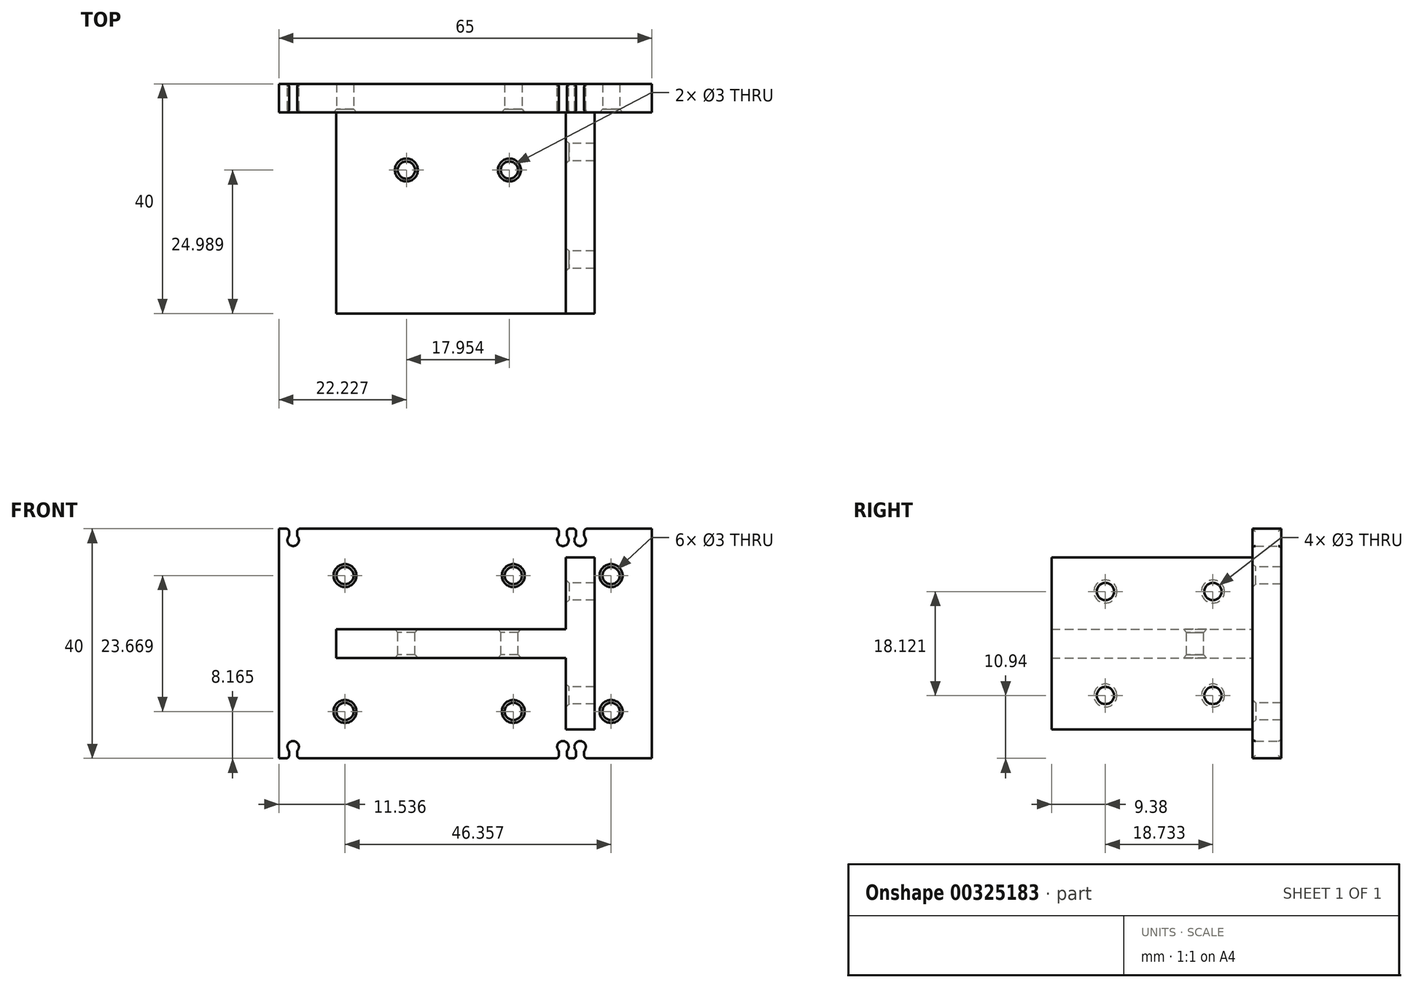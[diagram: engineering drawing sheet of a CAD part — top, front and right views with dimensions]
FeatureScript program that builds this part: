
annotation { "Feature Type Name" : "Feature", "Feature Type Description" : "" }
export const myFeature = defineFeature(function(context is Context, id is Id, definition is map)
    precondition{}
    {
        {
            var Q0;
            Q0=qCreatedBy(makeId("Front.planeOp"),FACE);
            var sketch = newSketch(context, id + "F0", { "sketchPlane" : qUnion([Q0])});
            skLineSegment(sketch, "E0.bottom", {"start": v(0, 0) * mm, "end": v(-55, 0) * mm});
            skLineSegment(sketch, "E0.top", {"start": v(0, 20) * mm, "end": v(-55, 20) * mm});
            skLineSegment(sketch, "E0.left", {"start": v(0, 0) * mm, "end": v(0, 20) * mm});
            skLineSegment(sketch, "E0.right", {"start": v(-55, 0) * mm, "end": v(-55, 20) * mm});
            skCircle(sketch, "E1", {"center": v(-52.5, 17.98) * mm, "radius": 1 * mm});
            skLineSegment(sketch, "E2", {"start": v(-52.5, 17.98) * mm, "end": v(-51.5, 17.98) * mm, "construction": true});
            skLineSegment(sketch, "E3", {"start": v(-52.5, 17.98) * mm, "end": v(-51.8, 18.69) * mm, "construction": true});
            skLineSegment(sketch, "E4", {"start": v(-51.8, 18.69) * mm, "end": v(-51.8, 20) * mm});
            skLineSegment(sketch, "E5", {"start": v(-53.2, 20) * mm, "end": v(-53.2, 18.69) * mm});
            skCircle(sketch, "E6", {"center": v(-2.5, 17.98) * mm, "radius": 1 * mm});
            skLineSegment(sketch, "E7", {"start": v(-2.5, 17.98) * mm, "end": v(-1.5, 17.98) * mm, "construction": true});
            skLineSegment(sketch, "E8", {"start": v(-2.5, 17.98) * mm, "end": v(-1.8, 18.69) * mm, "construction": true});
            skLineSegment(sketch, "E9", {"start": v(-1.8, 18.69) * mm, "end": v(-1.8, 20) * mm});
            skLineSegment(sketch, "E10", {"start": v(-3.2, 20) * mm, "end": v(-3.2, 18.69) * mm});
            skLineSegment(sketch, "E11.bottom", {"start": v(0, 0) * mm, "end": v(10, 0) * mm});
            skLineSegment(sketch, "E11.top", {"start": v(0, 20) * mm, "end": v(10, 20) * mm});
            skLineSegment(sketch, "E11.right", {"start": v(10, 0) * mm, "end": v(10, 20) * mm});
            skCircle(sketch, "E12", {"center": v(-5.5, 17.98) * mm, "radius": 1 * mm});
            skLineSegment(sketch, "E13", {"start": v(-5.5, 17.98) * mm, "end": v(-4.5, 17.98) * mm, "construction": true});
            skLineSegment(sketch, "E14", {"start": v(-5.5, 17.98) * mm, "end": v(-4.8, 18.69) * mm, "construction": true});
            skLineSegment(sketch, "E15", {"start": v(-4.8, 18.69) * mm, "end": v(-4.8, 20) * mm});
            skLineSegment(sketch, "E16", {"start": v(-6.2, 20) * mm, "end": v(-6.2, 18.69) * mm});
            skSolve(sketch);
        }
        {
            var Q0;
            Q0=makeQuery(id+"F0.imprint","IMPRINT",FACE,{"disambiguationData":[TD([[makeQuery(id+"F0.imprint","IMPRINT",EDGE,{"derivedFrom":sQuery(id+"F0.wireOp",EDGE,"E0.bottom")}),-1.0]])]});
            var Q1;
            Q1=makeQuery(id+"F0.imprint","IMPRINT",FACE,{"disambiguationData":[TD([[makeQuery(id+"F0.imprint","IMPRINT",EDGE,{"derivedFrom":sQuery(id+"F0.wireOp",EDGE,"E11.bottom")}),1.0]])]});
            extrude(context, id + "F1", {"entities" : qUnion([Q0, Q1]), "depth" : 5 * mm});
        }
        {
            var Q0;
            Q0=makeQuery(id+"F1.opExtrude","SWEPT_FACE",FACE,{"disambiguationData":[OSD([sQuery(id+"F0.wireOp",EDGE,"E4")])]});
            var Q1;
            Q1=makeQuery(id+"F1.opExtrude","SWEPT_FACE",FACE,{"disambiguationData":[OSD([sQuery(id+"F0.wireOp",EDGE,"E1")])]});
            var Q2;
            Q2=makeQuery(id+"F1.opExtrude","SWEPT_FACE",FACE,{"disambiguationData":[OSD([sQuery(id+"F0.wireOp",EDGE,"E5")])]});
            var Q3;
            Q3=makeQuery(id+"F1.opExtrude","CAP_EDGE",EDGE,{"disambiguationData":[OSD([sQuery(id+"F0.wireOp",EDGE,"E1")])],"isStart":false});
            var Q4;
            Q4=makeQuery(id+"F1.opExtrude","SWEPT_EDGE",EDGE,{"disambiguationData":[OSD([sQuery(id+"F0.wireOp",EDGE,"E0.top"),sQuery(id+"F0.wireOp",EDGE,"E4")])]});
            var Q5;
            Q5=makeQuery(id+"F1.opExtrude","SWEPT_EDGE",EDGE,{"disambiguationData":[OSD([sQuery(id+"F0.wireOp",EDGE,"E0.top"),sQuery(id+"F0.wireOp",EDGE,"E5")])]});
            var Q6;
            Q6=makeQuery(id+"F1.opExtrude","SWEPT_EDGE",EDGE,{"disambiguationData":[OSD([sQuery(id+"F0.wireOp",EDGE,"E1"),sQuery(id+"F0.wireOp",EDGE,"E5")])]});
            var Q7;
            Q7=makeQuery(id+"F1.opExtrude","SWEPT_EDGE",EDGE,{"disambiguationData":[OSD([sQuery(id+"F0.wireOp",EDGE,"E1"),sQuery(id+"F0.wireOp",EDGE,"E4")])]});
            var Q8;
            Q8=makeQuery(id+"F1.opExtrude","CAP_EDGE",EDGE,{"disambiguationData":[OSD([sQuery(id+"F0.wireOp",EDGE,"E5")])],"isStart":false});
            var Q9;
            Q9=makeQuery(id+"F1.opExtrude","CAP_EDGE",EDGE,{"disambiguationData":[OSD([sQuery(id+"F0.wireOp",EDGE,"E1")])],"isStart":true});
            var Q10;
            Q10=makeQuery(id+"F1.opExtrude","CAP_EDGE",EDGE,{"disambiguationData":[OSD([sQuery(id+"F0.wireOp",EDGE,"E4")])],"isStart":false});
            var Q11;
            Q11=makeQuery(id+"F1.opExtrude","CAP_EDGE",EDGE,{"disambiguationData":[OSD([sQuery(id+"F0.wireOp",EDGE,"E4")])],"isStart":true});
            var Q12;
            Q12=makeQuery(id+"F1.opExtrude","CAP_EDGE",EDGE,{"disambiguationData":[OSD([sQuery(id+"F0.wireOp",EDGE,"E5")])],"isStart":true});
            var Q13;
            Q13=makeQuery(id+"F1.opExtrude","SWEPT_FACE",FACE,{"disambiguationData":[OSD([sQuery(id+"F0.wireOp",EDGE,"E9")])]});
            var Q14;
            Q14=makeQuery(id+"F1.opExtrude","SWEPT_FACE",FACE,{"disambiguationData":[OSD([sQuery(id+"F0.wireOp",EDGE,"E10")])]});
            var Q15;
            Q15=makeQuery(id+"F1.opExtrude","CAP_EDGE",EDGE,{"disambiguationData":[OSD([sQuery(id+"F0.wireOp",EDGE,"E6")])],"isStart":false});
            var Q16;
            Q16=makeQuery(id+"F1.opExtrude","SWEPT_FACE",FACE,{"disambiguationData":[OSD([sQuery(id+"F0.wireOp",EDGE,"E6")])]});
            var Q17;
            Q17=makeQuery(id+"F1.opExtrude","SWEPT_EDGE",EDGE,{"disambiguationData":[OSD([sQuery(id+"F0.wireOp",EDGE,"E6"),sQuery(id+"F0.wireOp",EDGE,"E9")])]});
            var Q18;
            Q18=makeQuery(id+"F1.opExtrude","SWEPT_EDGE",EDGE,{"disambiguationData":[OSD([sQuery(id+"F0.wireOp",EDGE,"E6"),sQuery(id+"F0.wireOp",EDGE,"E10")])]});
            var Q19;
            Q19=makeQuery(id+"F1.opExtrude","SWEPT_EDGE",EDGE,{"disambiguationData":[OSD([sQuery(id+"F0.wireOp",EDGE,"E0.top"),sQuery(id+"F0.wireOp",EDGE,"E9")])]});
            var Q20;
            Q20=makeQuery(id+"F1.opExtrude","SWEPT_EDGE",EDGE,{"disambiguationData":[OSD([sQuery(id+"F0.wireOp",EDGE,"E0.top"),sQuery(id+"F0.wireOp",EDGE,"E10")])]});
            var Q21;
            Q21=makeQuery(id+"F1.opExtrude","CAP_EDGE",EDGE,{"disambiguationData":[OSD([sQuery(id+"F0.wireOp",EDGE,"E6")])],"isStart":true});
            var Q22;
            Q22=makeQuery(id+"F1.opExtrude","CAP_EDGE",EDGE,{"disambiguationData":[OSD([sQuery(id+"F0.wireOp",EDGE,"E9")])],"isStart":false});
            var Q23;
            Q23=makeQuery(id+"F1.opExtrude","CAP_EDGE",EDGE,{"disambiguationData":[OSD([sQuery(id+"F0.wireOp",EDGE,"E10")])],"isStart":false});
            var Q24;
            Q24=makeQuery(id+"F1.opExtrude","CAP_EDGE",EDGE,{"disambiguationData":[OSD([sQuery(id+"F0.wireOp",EDGE,"E9")])],"isStart":true});
            var Q25;
            Q25=makeQuery(id+"F1.opExtrude","CAP_EDGE",EDGE,{"disambiguationData":[OSD([sQuery(id+"F0.wireOp",EDGE,"E10")])],"isStart":true});
            var Q26;
            Q26=makeQuery(id+"F1.opExtrude","CAP_EDGE",EDGE,{"disambiguationData":[OSD([sQuery(id+"F0.wireOp",EDGE,"E12")])],"isStart":false});
            var Q27;
            Q27=makeQuery(id+"F1.opExtrude","CAP_EDGE",EDGE,{"disambiguationData":[OSD([sQuery(id+"F0.wireOp",EDGE,"E12")])],"isStart":true});
            var Q28;
            Q28=makeQuery(id+"F1.opExtrude","CAP_EDGE",EDGE,{"disambiguationData":[OSD([sQuery(id+"F0.wireOp",EDGE,"E15")])],"isStart":false});
            var Q29;
            Q29=makeQuery(id+"F1.opExtrude","SWEPT_EDGE",EDGE,{"disambiguationData":[OSD([sQuery(id+"F0.wireOp",EDGE,"E0.top"),sQuery(id+"F0.wireOp",EDGE,"E15")])]});
            var Q30;
            Q30=makeQuery(id+"F1.opExtrude","SWEPT_EDGE",EDGE,{"disambiguationData":[OSD([sQuery(id+"F0.wireOp",EDGE,"E0.top"),sQuery(id+"F0.wireOp",EDGE,"E16")])]});
            var Q31;
            Q31=makeQuery(id+"F1.opExtrude","CAP_EDGE",EDGE,{"disambiguationData":[OSD([sQuery(id+"F0.wireOp",EDGE,"E16")])],"isStart":false});
            var Q32;
            Q32=makeQuery(id+"F1.opExtrude","CAP_EDGE",EDGE,{"disambiguationData":[OSD([sQuery(id+"F0.wireOp",EDGE,"E16")])],"isStart":true});
            var Q33;
            Q33=makeQuery(id+"F1.opExtrude","SWEPT_EDGE",EDGE,{"disambiguationData":[OSD([sQuery(id+"F0.wireOp",EDGE,"E12"),sQuery(id+"F0.wireOp",EDGE,"E16")])]});
            var Q34;
            Q34=makeQuery(id+"F1.opExtrude","SWEPT_EDGE",EDGE,{"disambiguationData":[OSD([sQuery(id+"F0.wireOp",EDGE,"E12"),sQuery(id+"F0.wireOp",EDGE,"E15")])]});
            var Q35;
            Q35=makeQuery(id+"F1.opExtrude","CAP_EDGE",EDGE,{"disambiguationData":[OSD([sQuery(id+"F0.wireOp",EDGE,"E15")])],"isStart":true});
            fillet(context, id + "F2", {"entities" : qUnion([Q0, Q1, Q2, Q3, Q4, Q5, Q6, Q7, Q8, Q9, Q10, Q11, Q12, Q13, Q14, Q15, Q16, Q17, Q18, Q19, Q20, Q21, Q22, Q23, Q24, Q25, Q26, Q27, Q28, Q29, Q30, Q31, Q32, Q33, Q34, Q35]), "radius" : 0.5 * mm, "tangentPropagation" : true, "allowEdgeOverflow" : false});
        }
        {
            var Q0;
            Q0=makeQuery(id+"F1.opExtrude","CAP_FACE",FACE,{"disambiguationData":[OSD([sQuery(id+"F0.wireOp",EDGE,"E0.bottom"),sQuery(id+"F0.wireOp",EDGE,"E0.top"),sQuery(id+"F0.wireOp",EDGE,"E0.right"),sQuery(id+"F0.wireOp",EDGE,"E1"),sQuery(id+"F0.wireOp",EDGE,"E4"),sQuery(id+"F0.wireOp",EDGE,"E5"),sQuery(id+"F0.wireOp",EDGE,"E6"),sQuery(id+"F0.wireOp",EDGE,"E9"),sQuery(id+"F0.wireOp",EDGE,"E10"),sQuery(id+"F0.wireOp",EDGE,"E11.bottom"),sQuery(id+"F0.wireOp",EDGE,"E11.top"),sQuery(id+"F0.wireOp",EDGE,"E11.right")])],"isStart":false});
            var sketch = newSketch(context, id + "F3", { "sketchPlane" : qUnion([Q0])});
            skLineSegment(sketch, "E17.bottom", {"start": v(0, 0) * mm, "end": v(-5, 0) * mm});
            skLineSegment(sketch, "E17.top", {"start": v(0, 15) * mm, "end": v(-5, 15) * mm});
            skLineSegment(sketch, "E17.left", {"start": v(0, 0) * mm, "end": v(0, 15) * mm});
            skLineSegment(sketch, "E17.right", {"start": v(-5, 0) * mm, "end": v(-5, 15) * mm});
            skLineSegment(sketch, "E18.bottom", {"start": v(-5, 0) * mm, "end": v(-45, 0) * mm});
            skLineSegment(sketch, "E18.top", {"start": v(-5, 2.5) * mm, "end": v(-45, 2.5) * mm});
            skLineSegment(sketch, "E18.left", {"start": v(-5, 0) * mm, "end": v(-5, 2.5) * mm});
            skLineSegment(sketch, "E18.right", {"start": v(-45, 0) * mm, "end": v(-45, 2.5) * mm});
            skSolve(sketch);
        }
        {
            var Q0;
            Q0=makeQuery(id+"F3.imprint","IMPRINT",FACE,{"disambiguationData":[TD([[makeQuery(id+"F3.imprint","IMPRINT",EDGE,{"derivedFrom":sQuery(id+"F3.wireOp",EDGE,"E17.bottom")}),-1.0]])]});
            var Q1;
            Q1=makeQuery(id+"F3.imprint","IMPRINT",FACE,{"disambiguationData":[TD([[makeQuery(id+"F3.imprint","IMPRINT",EDGE,{"derivedFrom":sQuery(id+"F3.wireOp",EDGE,"E18.bottom")}),-1.0]])]});
            extrude(context, id + "F4", {"entities" : qUnion([Q0, Q1]), "operationType" : NewBodyOperationType.ADD, "depth" : 35 * mm});
        }
        {
            var Q0;
            Q0=makeQuery(id+"F1.opExtrude","CAP_FACE",FACE,{"disambiguationData":[OSD([sQuery(id+"F0.wireOp",EDGE,"E0.bottom"),sQuery(id+"F0.wireOp",EDGE,"E0.top"),sQuery(id+"F0.wireOp",EDGE,"E0.left"),sQuery(id+"F0.wireOp",EDGE,"E0.right"),sQuery(id+"F0.wireOp",EDGE,"E1"),sQuery(id+"F0.wireOp",EDGE,"E4"),sQuery(id+"F0.wireOp",EDGE,"E5"),sQuery(id+"F0.wireOp",EDGE,"E6"),sQuery(id+"F0.wireOp",EDGE,"E9"),sQuery(id+"F0.wireOp",EDGE,"E10")])],"isStart":false});
            var sketch = newSketch(context, id + "F5", { "sketchPlane" : qUnion([Q0])});
            skLineSegment(sketch, "E19", {"start": v(-43.46, 11.83) * mm, "end": v(-14.14, 11.83) * mm, "construction": true});
            skLineSegment(sketch, "E20", {"start": v(-14.14, 11.83) * mm, "end": v(2.9, 11.83) * mm, "construction": true});
            skSolve(sketch);
        }
        {
            var Q0;
            Q0=makeQuery(id+"F4.opExtrude","SWEPT_FACE",FACE,{"disambiguationData":[OSD([sQuery(id+"F3.wireOp",EDGE,"E17.right")])]});
            var sketch = newSketch(context, id + "F6", { "sketchPlane" : qUnion([Q0])});
            skLineSegment(sketch, "E21", {"start": v(11.89, 9.06) * mm, "end": v(30.62, 9.06) * mm, "construction": true});
            skSolve(sketch);
        }
        {
            var Q0;
            Q0=makeQuery(id+"F4.opExtrude","SWEPT_FACE",FACE,{"disambiguationData":[OSD([sQuery(id+"F3.wireOp",EDGE,"E18.top")])]});
            var sketch = newSketch(context, id + "F7", { "sketchPlane" : qUnion([Q0])});
            skLineSegment(sketch, "E22", {"start": v(-32.77, -15.01) * mm, "end": v(-14.82, -15.01) * mm, "construction": true});
            skSolve(sketch);
        }
        {
            var Q0;
            Q0=sQuery(id+"F5.wireOp",VERTEX,"E19.start");
            var Q1;
            Q1=sQuery(id+"F5.wireOp",VERTEX,"E19.end");
            var Q2;
            Q2=sQuery(id+"F5.wireOp",VERTEX,"E20.end");
            var Q3;
            Q3=sQuery(id+"F7.wireOp",VERTEX,"E22.start");
            var Q4;
            Q4=sQuery(id+"F7.wireOp",VERTEX,"E22.end");
            var Q5;
            Q5=sQuery(id+"F6.wireOp",VERTEX,"E21.start");
            var Q6;
            Q6=sQuery(id+"F6.wireOp",VERTEX,"E21.end");
            var Q7;
            Q7=makeQuery(id+"F1.opExtrude","SWEPT_BODY",BODY,{"disambiguationData":[OSD([sQuery(id+"F0.wireOp",EDGE,"E0.bottom"),sQuery(id+"F0.wireOp",EDGE,"E0.top"),sQuery(id+"F0.wireOp",EDGE,"E0.left"),sQuery(id+"F0.wireOp",EDGE,"E0.right"),sQuery(id+"F0.wireOp",EDGE,"E1"),sQuery(id+"F0.wireOp",EDGE,"E4"),sQuery(id+"F0.wireOp",EDGE,"E5"),sQuery(id+"F0.wireOp",EDGE,"E6"),sQuery(id+"F0.wireOp",EDGE,"E9"),sQuery(id+"F0.wireOp",EDGE,"E10")])]});
            hole(context, id + "F8", {"style" : HoleStyle.C_SINK, "endStyle" : HoleEndStyle.THROUGH, "holeDiameter" : 3 * mm, "cSinkDiameter" : 4 * mm, "cSinkAngle" : 82 * degree, "tappedDepth" : 12 * mm, "tapClearance" : 3, "locations" : qUnion([Q0, Q1, Q2, Q3, Q4, Q5, Q6]), "scope" : qUnion([Q7])});
        }
        {
            var Q0;
            Q0=makeQuery(id+"F1.opExtrude","SWEPT_BODY",BODY,{"disambiguationData":[OSD([sQuery(id+"F0.wireOp",EDGE,"E0.bottom"),sQuery(id+"F0.wireOp",EDGE,"E0.top"),sQuery(id+"F0.wireOp",EDGE,"E0.right"),sQuery(id+"F0.wireOp",EDGE,"E1"),sQuery(id+"F0.wireOp",EDGE,"E4"),sQuery(id+"F0.wireOp",EDGE,"E5"),sQuery(id+"F0.wireOp",EDGE,"E6"),sQuery(id+"F0.wireOp",EDGE,"E9"),sQuery(id+"F0.wireOp",EDGE,"E10"),sQuery(id+"F0.wireOp",EDGE,"E11.bottom"),sQuery(id+"F0.wireOp",EDGE,"E11.top"),sQuery(id+"F0.wireOp",EDGE,"E11.right")])]});
            var Q1;
            Q1=makeQuery(id+"F4.opExtrude","SWEPT_BODY",BODY,{"disambiguationData":[OSD([sQuery(id+"F3.wireOp",EDGE,"E17.bottom"),sQuery(id+"F3.wireOp",EDGE,"E17.top"),sQuery(id+"F3.wireOp",EDGE,"E17.left"),sQuery(id+"F3.wireOp",EDGE,"E17.right"),sQuery(id+"F3.wireOp",EDGE,"E18.bottom"),sQuery(id+"F3.wireOp",EDGE,"E18.top"),sQuery(id+"F3.wireOp",EDGE,"E18.right")])]});
            var Q2;
            Q2=makeQuery(id+"F1.opExtrude","SWEPT_FACE",FACE,{"disambiguationData":[OSD([sQuery(id+"F0.wireOp",EDGE,"E0.bottom")])]});
            mirror(context, id + "F9", {"operationType" : NewBodyOperationType.ADD, "entities" : qUnion([Q0, Q1]), "mirrorPlane" : qUnion([Q2])});
        }
    });
